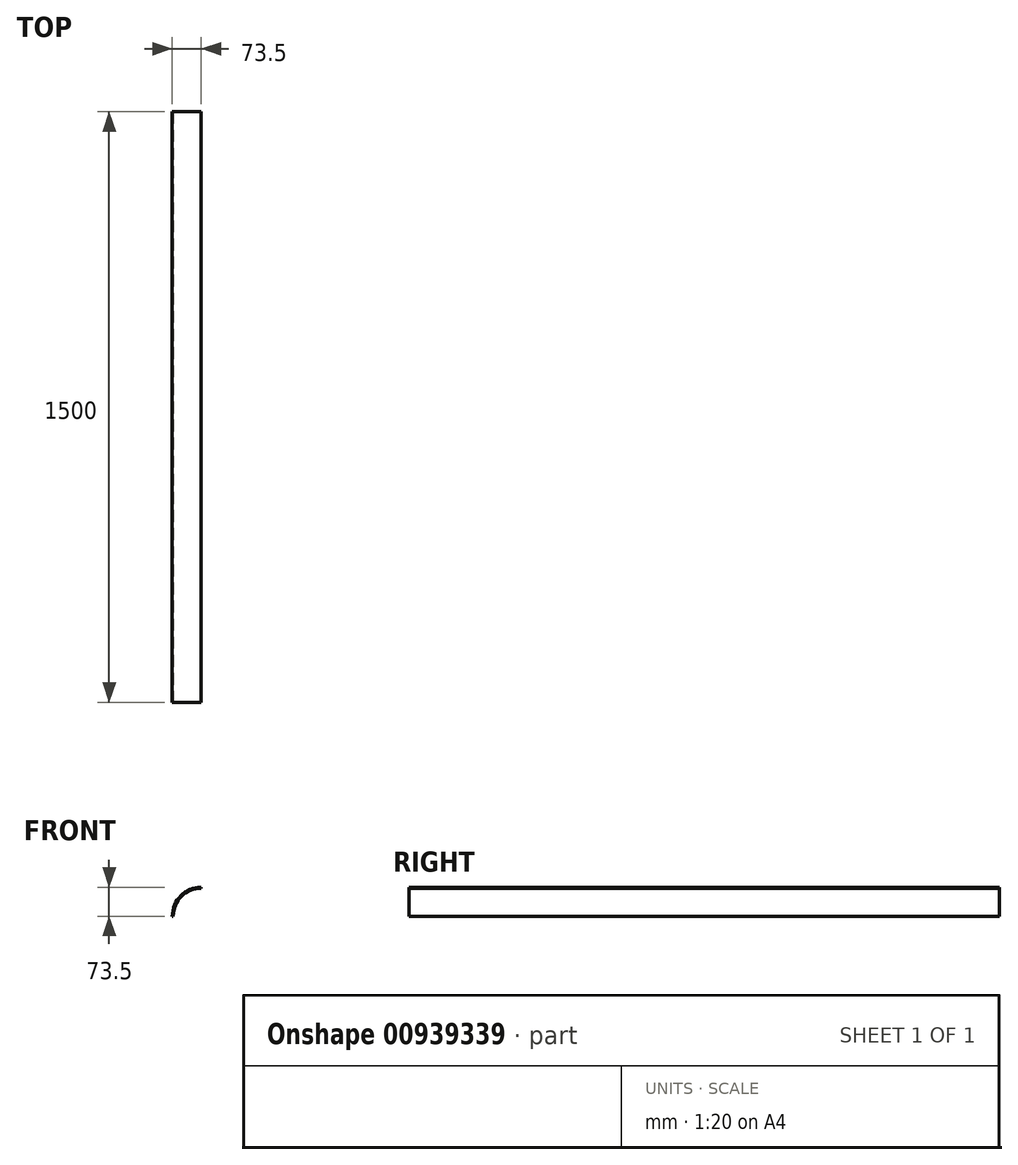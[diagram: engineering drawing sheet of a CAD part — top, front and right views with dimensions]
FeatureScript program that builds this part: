
annotation { "Feature Type Name" : "Feature", "Feature Type Description" : "" }
export const myFeature = defineFeature(function(context is Context, id is Id, definition is map)
    precondition{}
    {
        {
            var Q0;
            Q0=qCreatedBy(makeId("Front.planeOp"),FACE);
            var sketch = newSketch(context, id + "F0", { "sketchPlane" : qUnion([Q0])});
            skLineSegment(sketch, "E0", {"start": v(-32.44, -41.06) * mm, "end": v(-29.94, -41.06) * mm});
            skArc(sketch, "E1", {"start": v(41.06, 32.44) * mm, "mid": v(-10.91, 10.91) * mm, "end": v(-32.44, -41.06) * mm});
            skLineSegment(sketch, "E2", {"start": v(41.06, 32.44) * mm, "end": v(41.06, 29.94) * mm});
            skArc(sketch, "E3.0", {"start": v(41.06, 29.94) * mm, "mid": v(-9.14, 9.14) * mm, "end": v(-29.94, -41.06) * mm});
            skSolve(sketch);
        }
        {
            var Q0;
            Q0=sQuery(id+"F0.wireOp",EDGE,"E0");
            var Q1;
            Q1=sQuery(id+"F0.wireOp",EDGE,"E1");
            var Q2;
            Q2=sQuery(id+"F0.wireOp",EDGE,"E2");
            var Q3;
            Q3=sQuery(id+"F0.wireOp",EDGE,"E3.0");
            extrude(context, id + "F1", {"bodyType" : ToolBodyType.SURFACE, "surfaceEntities" : qUnion([Q0, Q1, Q2, Q3]), "depth" : 1500 * mm, "offsetDistance" : 25 * mm});
        }
    });
